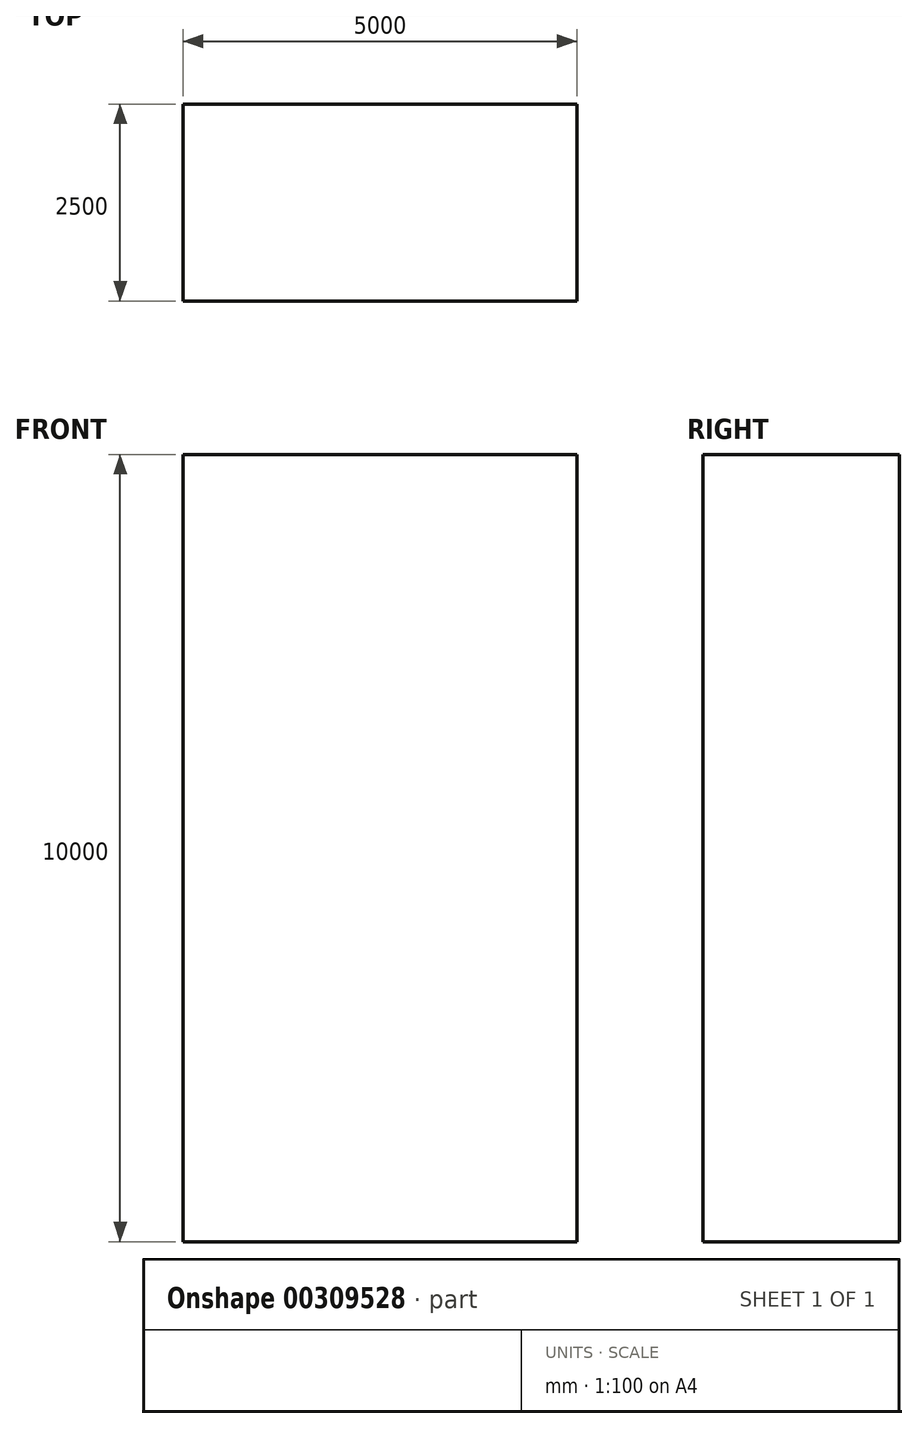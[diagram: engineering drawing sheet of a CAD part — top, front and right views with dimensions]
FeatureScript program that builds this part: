
annotation { "Feature Type Name" : "Feature", "Feature Type Description" : "" }
export const myFeature = defineFeature(function(context is Context, id is Id, definition is map)
    precondition{}
    {
        {
            var Q0;
            Q0=qCreatedBy(makeId("Front.planeOp"),FACE);
            var sketch = newSketch(context, id + "F0", { "sketchPlane" : qUnion([Q0])});
            skLineSegment(sketch, "E0.bottom", {"start": v(0, 0) * mm, "end": v(5000, 0) * mm});
            skLineSegment(sketch, "E0.top", {"start": v(0, 10000) * mm, "end": v(5000, 10000) * mm});
            skLineSegment(sketch, "E0.left", {"start": v(0, 0) * mm, "end": v(0, 10000) * mm});
            skLineSegment(sketch, "E0.right", {"start": v(5000, 0) * mm, "end": v(5000, 10000) * mm});
            skSolve(sketch);
        }
        {
            var Q0;
            Q0=makeQuery(id+"F0.imprint","IMPRINT",FACE,{"disambiguationData":[TD([[makeQuery(id+"F0.imprint","IMPRINT",EDGE,{"derivedFrom":sQuery(id+"F0.wireOp",EDGE,"E0.bottom")}),1.0]])]});
            extrude(context, id + "F1", {"entities" : qUnion([Q0]), "depth" : 2500 * mm});
        }
    });
